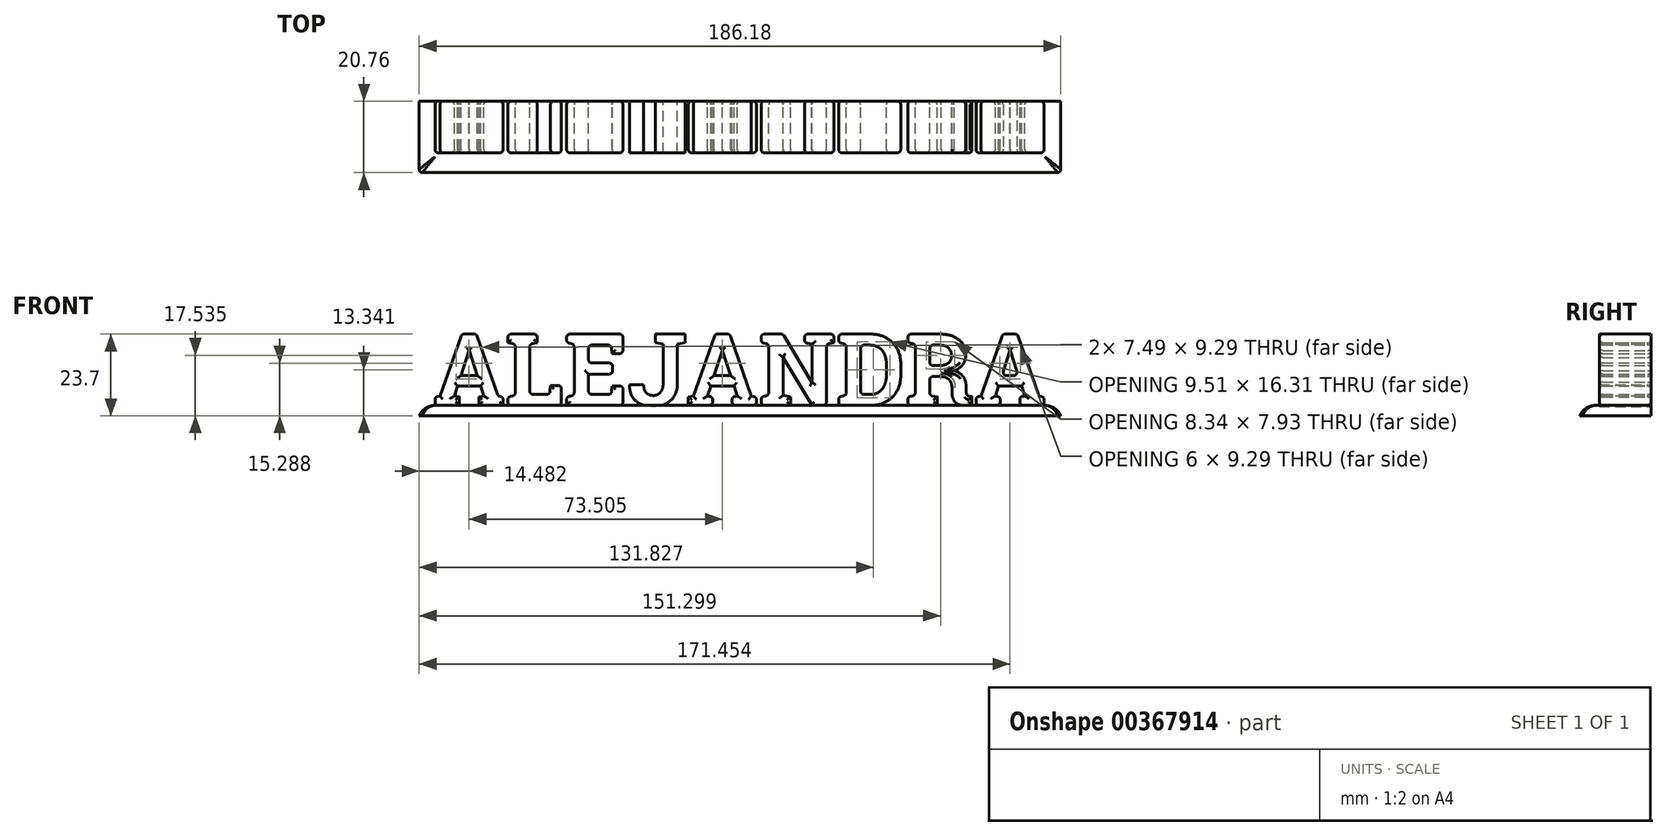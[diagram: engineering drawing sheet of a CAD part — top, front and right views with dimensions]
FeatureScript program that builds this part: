
annotation { "Feature Type Name" : "Feature", "Feature Type Description" : "" }
export const myFeature = defineFeature(function(context is Context, id is Id, definition is map)
    precondition{}
    {
        {
            var Q0;
            Q0=qCreatedBy(makeId("Front.planeOp"),FACE);
            var sketch = newSketch(context, id + "F0", { "sketchPlane" : qUnion([Q0])});
            skText(sketch, "E0", { "text": "ALEJANDRA", "fontName": "RobotoSlab-Bold.ttf"});
            const initialGuessF0  = {"E0": [-0.08954, 0, 1, 0, 0.02096]};
            skSetInitialGuess(sketch, initialGuessF0);
            skSolve(sketch);
        }
        {
            var Q0;
            Q0 = qSketchRegion(id + "F0", true);
            extrude(context, id + "F1", {"entities" : qUnion([Q0]), "depth" : 15 * mm});
        }
        {
            var Q0;
            Q0=makeQuery(id+"F1.opExtrude","SWEPT_FACE",FACE,{"disambiguationData":[OSD([sQuery(id+"F0.wireOp",EDGE,"E0.sketch_text.stroke-42")])]});
            var sketch = newSketch(context, id + "F2", { "sketchPlane" : qUnion([Q0])});
            skLineSegment(sketch, "E1.bottom", {"start": v(-93.56, 20.7) * mm, "end": v(92.62, 20.7) * mm});
            skLineSegment(sketch, "E1.top", {"start": v(-93.56, 0) * mm, "end": v(92.62, 0) * mm});
            skLineSegment(sketch, "E1.left", {"start": v(-93.56, 20.7) * mm, "end": v(-93.56, 0) * mm});
            skLineSegment(sketch, "E1.right", {"start": v(92.62, 20.7) * mm, "end": v(92.62, 0) * mm});
            skSolve(sketch);
        }
        {
            var Q0;
            Q0 = qSketchRegion(id + "F2", true);
            extrude(context, id + "F3", {"entities" : qUnion([Q0]), "depth" : 3 * mm});
        }
        {
            var Q0;
            Q0=makeQuery(id+"F3.opExtrude","CAP_EDGE",EDGE,{"disambiguationData":[OSD([sQuery(id+"F2.wireOp",EDGE,"E1.bottom")])],"isStart":true});
            var Q1;
            Q1=makeQuery(id+"F3.opExtrude","CAP_EDGE",EDGE,{"disambiguationData":[OSD([sQuery(id+"F2.wireOp",EDGE,"E1.right")])],"isStart":true});
            var Q2;
            Q2=makeQuery(id+"F3.opExtrude","CAP_EDGE",EDGE,{"disambiguationData":[OSD([sQuery(id+"F2.wireOp",EDGE,"E1.left")])],"isStart":true});
            fillet(context, id + "F4", {"entities" : qUnion([Q0, Q1, Q2]), "radius" : 5 * mm, "tangentPropagation" : true, "allowEdgeOverflow" : false});
        }
        {
            var Q0;
            Q0=makeQuery(id+"F1.opExtrude","CAP_FACE",FACE,{"disambiguationData":[OSD([sQuery(id+"F0.wireOp",EDGE,"E0.sketch_text.stroke-36"),sQuery(id+"F0.wireOp",EDGE,"E0.sketch_text.stroke-37"),sQuery(id+"F0.wireOp",EDGE,"E0.sketch_text.stroke-38"),sQuery(id+"F0.wireOp",EDGE,"E0.sketch_text.stroke-39"),sQuery(id+"F0.wireOp",EDGE,"E0.sketch_text.stroke-40"),sQuery(id+"F0.wireOp",EDGE,"E0.sketch_text.stroke-41"),sQuery(id+"F0.wireOp",EDGE,"E0.sketch_text.stroke-42"),sQuery(id+"F0.wireOp",EDGE,"E0.sketch_text.stroke-43"),sQuery(id+"F0.wireOp",EDGE,"E0.sketch_text.stroke-44"),sQuery(id+"F0.wireOp",EDGE,"E0.sketch_text.stroke-45"),sQuery(id+"F0.wireOp",EDGE,"E0.sketch_text.stroke-46"),sQuery(id+"F0.wireOp",EDGE,"E0.sketch_text.stroke-47"),sQuery(id+"F0.wireOp",EDGE,"E0.sketch_text.stroke-48"),sQuery(id+"F0.wireOp",EDGE,"E0.sketch_text.stroke-49"),sQuery(id+"F0.wireOp",EDGE,"E0.sketch_text.stroke-50"),sQuery(id+"F0.wireOp",EDGE,"E0.sketch_text.stroke-51"),sQuery(id+"F0.wireOp",EDGE,"E0.sketch_text.stroke-52"),sQuery(id+"F0.wireOp",EDGE,"E0.sketch_text.stroke-53"),sQuery(id+"F0.wireOp",EDGE,"E0.sketch_text.stroke-54"),sQuery(id+"F0.wireOp",EDGE,"E0.sketch_text.stroke-55"),sQuery(id+"F0.wireOp",EDGE,"E0.sketch_text.stroke-56")])],"isStart":false});
            var Q1;
            Q1=makeQuery(id+"F1.opExtrude","CAP_FACE",FACE,{"disambiguationData":[OSD([sQuery(id+"F0.wireOp",EDGE,"E0.sketch_text.stroke-20"),sQuery(id+"F0.wireOp",EDGE,"E0.sketch_text.stroke-21"),sQuery(id+"F0.wireOp",EDGE,"E0.sketch_text.stroke-22"),sQuery(id+"F0.wireOp",EDGE,"E0.sketch_text.stroke-23"),sQuery(id+"F0.wireOp",EDGE,"E0.sketch_text.stroke-24"),sQuery(id+"F0.wireOp",EDGE,"E0.sketch_text.stroke-25"),sQuery(id+"F0.wireOp",EDGE,"E0.sketch_text.stroke-26"),sQuery(id+"F0.wireOp",EDGE,"E0.sketch_text.stroke-27"),sQuery(id+"F0.wireOp",EDGE,"E0.sketch_text.stroke-28"),sQuery(id+"F0.wireOp",EDGE,"E0.sketch_text.stroke-29"),sQuery(id+"F0.wireOp",EDGE,"E0.sketch_text.stroke-30"),sQuery(id+"F0.wireOp",EDGE,"E0.sketch_text.stroke-31"),sQuery(id+"F0.wireOp",EDGE,"E0.sketch_text.stroke-32"),sQuery(id+"F0.wireOp",EDGE,"E0.sketch_text.stroke-33"),sQuery(id+"F0.wireOp",EDGE,"E0.sketch_text.stroke-34"),sQuery(id+"F0.wireOp",EDGE,"E0.sketch_text.stroke-35")])],"isStart":false});
            var Q2;
            Q2=makeQuery(id+"F1.opExtrude","CAP_FACE",FACE,{"disambiguationData":[OSD([sQuery(id+"F0.wireOp",EDGE,"E0.sketch_text.stroke-0"),sQuery(id+"F0.wireOp",EDGE,"E0.sketch_text.stroke-1"),sQuery(id+"F0.wireOp",EDGE,"E0.sketch_text.stroke-2"),sQuery(id+"F0.wireOp",EDGE,"E0.sketch_text.stroke-3"),sQuery(id+"F0.wireOp",EDGE,"E0.sketch_text.stroke-4"),sQuery(id+"F0.wireOp",EDGE,"E0.sketch_text.stroke-5"),sQuery(id+"F0.wireOp",EDGE,"E0.sketch_text.stroke-6"),sQuery(id+"F0.wireOp",EDGE,"E0.sketch_text.stroke-7"),sQuery(id+"F0.wireOp",EDGE,"E0.sketch_text.stroke-8"),sQuery(id+"F0.wireOp",EDGE,"E0.sketch_text.stroke-9"),sQuery(id+"F0.wireOp",EDGE,"E0.sketch_text.stroke-10"),sQuery(id+"F0.wireOp",EDGE,"E0.sketch_text.stroke-11"),sQuery(id+"F0.wireOp",EDGE,"E0.sketch_text.stroke-12"),sQuery(id+"F0.wireOp",EDGE,"E0.sketch_text.stroke-13"),sQuery(id+"F0.wireOp",EDGE,"E0.sketch_text.stroke-14"),sQuery(id+"F0.wireOp",EDGE,"E0.sketch_text.stroke-15"),sQuery(id+"F0.wireOp",EDGE,"E0.sketch_text.stroke-16"),sQuery(id+"F0.wireOp",EDGE,"E0.sketch_text.stroke-17"),sQuery(id+"F0.wireOp",EDGE,"E0.sketch_text.stroke-18"),sQuery(id+"F0.wireOp",EDGE,"E0.sketch_text.stroke-19")])],"isStart":false});
            var Q3;
            Q3=makeQuery(id+"F1.opExtrude","CAP_EDGE",EDGE,{"disambiguationData":[OSD([sQuery(id+"F0.wireOp",EDGE,"E0.sketch_text.stroke-70")])],"isStart":false});
            var Q4;
            Q4=makeQuery(id+"F1.opExtrude","CAP_EDGE",EDGE,{"disambiguationData":[OSD([sQuery(id+"F0.wireOp",EDGE,"E0.sketch_text.stroke-59")])],"isStart":false});
            var Q5;
            Q5=makeQuery(id+"F1.opExtrude","CAP_FACE",FACE,{"disambiguationData":[OSD([sQuery(id+"F0.wireOp",EDGE,"E0.sketch_text.stroke-75"),sQuery(id+"F0.wireOp",EDGE,"E0.sketch_text.stroke-76"),sQuery(id+"F0.wireOp",EDGE,"E0.sketch_text.stroke-77"),sQuery(id+"F0.wireOp",EDGE,"E0.sketch_text.stroke-78"),sQuery(id+"F0.wireOp",EDGE,"E0.sketch_text.stroke-79"),sQuery(id+"F0.wireOp",EDGE,"E0.sketch_text.stroke-80"),sQuery(id+"F0.wireOp",EDGE,"E0.sketch_text.stroke-81"),sQuery(id+"F0.wireOp",EDGE,"E0.sketch_text.stroke-82"),sQuery(id+"F0.wireOp",EDGE,"E0.sketch_text.stroke-83"),sQuery(id+"F0.wireOp",EDGE,"E0.sketch_text.stroke-84"),sQuery(id+"F0.wireOp",EDGE,"E0.sketch_text.stroke-85"),sQuery(id+"F0.wireOp",EDGE,"E0.sketch_text.stroke-86"),sQuery(id+"F0.wireOp",EDGE,"E0.sketch_text.stroke-87"),sQuery(id+"F0.wireOp",EDGE,"E0.sketch_text.stroke-88"),sQuery(id+"F0.wireOp",EDGE,"E0.sketch_text.stroke-89"),sQuery(id+"F0.wireOp",EDGE,"E0.sketch_text.stroke-90"),sQuery(id+"F0.wireOp",EDGE,"E0.sketch_text.stroke-91"),sQuery(id+"F0.wireOp",EDGE,"E0.sketch_text.stroke-92"),sQuery(id+"F0.wireOp",EDGE,"E0.sketch_text.stroke-93"),sQuery(id+"F0.wireOp",EDGE,"E0.sketch_text.stroke-94")])],"isStart":false});
            var Q6;
            Q6=makeQuery(id+"F1.opExtrude","CAP_FACE",FACE,{"disambiguationData":[OSD([sQuery(id+"F0.wireOp",EDGE,"E0.sketch_text.stroke-95"),sQuery(id+"F0.wireOp",EDGE,"E0.sketch_text.stroke-96"),sQuery(id+"F0.wireOp",EDGE,"E0.sketch_text.stroke-97"),sQuery(id+"F0.wireOp",EDGE,"E0.sketch_text.stroke-98"),sQuery(id+"F0.wireOp",EDGE,"E0.sketch_text.stroke-99"),sQuery(id+"F0.wireOp",EDGE,"E0.sketch_text.stroke-100"),sQuery(id+"F0.wireOp",EDGE,"E0.sketch_text.stroke-101"),sQuery(id+"F0.wireOp",EDGE,"E0.sketch_text.stroke-102"),sQuery(id+"F0.wireOp",EDGE,"E0.sketch_text.stroke-103"),sQuery(id+"F0.wireOp",EDGE,"E0.sketch_text.stroke-104"),sQuery(id+"F0.wireOp",EDGE,"E0.sketch_text.stroke-105"),sQuery(id+"F0.wireOp",EDGE,"E0.sketch_text.stroke-106"),sQuery(id+"F0.wireOp",EDGE,"E0.sketch_text.stroke-107"),sQuery(id+"F0.wireOp",EDGE,"E0.sketch_text.stroke-108"),sQuery(id+"F0.wireOp",EDGE,"E0.sketch_text.stroke-109"),sQuery(id+"F0.wireOp",EDGE,"E0.sketch_text.stroke-110"),sQuery(id+"F0.wireOp",EDGE,"E0.sketch_text.stroke-111"),sQuery(id+"F0.wireOp",EDGE,"E0.sketch_text.stroke-112"),sQuery(id+"F0.wireOp",EDGE,"E0.sketch_text.stroke-113"),sQuery(id+"F0.wireOp",EDGE,"E0.sketch_text.stroke-114"),sQuery(id+"F0.wireOp",EDGE,"E0.sketch_text.stroke-115"),sQuery(id+"F0.wireOp",EDGE,"E0.sketch_text.stroke-116"),sQuery(id+"F0.wireOp",EDGE,"E0.sketch_text.stroke-117"),sQuery(id+"F0.wireOp",EDGE,"E0.sketch_text.stroke-118")])],"isStart":false});
            var Q7;
            Q7=makeQuery(id+"F1.opExtrude","CAP_FACE",FACE,{"disambiguationData":[OSD([sQuery(id+"F0.wireOp",EDGE,"E0.sketch_text.stroke-119"),sQuery(id+"F0.wireOp",EDGE,"E0.sketch_text.stroke-120"),sQuery(id+"F0.wireOp",EDGE,"E0.sketch_text.stroke-121"),sQuery(id+"F0.wireOp",EDGE,"E0.sketch_text.stroke-122"),sQuery(id+"F0.wireOp",EDGE,"E0.sketch_text.stroke-123"),sQuery(id+"F0.wireOp",EDGE,"E0.sketch_text.stroke-124"),sQuery(id+"F0.wireOp",EDGE,"E0.sketch_text.stroke-125"),sQuery(id+"F0.wireOp",EDGE,"E0.sketch_text.stroke-126"),sQuery(id+"F0.wireOp",EDGE,"E0.sketch_text.stroke-127"),sQuery(id+"F0.wireOp",EDGE,"E0.sketch_text.stroke-128"),sQuery(id+"F0.wireOp",EDGE,"E0.sketch_text.stroke-129"),sQuery(id+"F0.wireOp",EDGE,"E0.sketch_text.stroke-130"),sQuery(id+"F0.wireOp",EDGE,"E0.sketch_text.stroke-131"),sQuery(id+"F0.wireOp",EDGE,"E0.sketch_text.stroke-132"),sQuery(id+"F0.wireOp",EDGE,"E0.sketch_text.stroke-133"),sQuery(id+"F0.wireOp",EDGE,"E0.sketch_text.stroke-134"),sQuery(id+"F0.wireOp",EDGE,"E0.sketch_text.stroke-135"),sQuery(id+"F0.wireOp",EDGE,"E0.sketch_text.stroke-136"),sQuery(id+"F0.wireOp",EDGE,"E0.sketch_text.stroke-137"),sQuery(id+"F0.wireOp",EDGE,"E0.sketch_text.stroke-138"),sQuery(id+"F0.wireOp",EDGE,"E0.sketch_text.stroke-139")])],"isStart":false});
            var Q8;
            Q8=makeQuery(id+"F1.opExtrude","CAP_FACE",FACE,{"disambiguationData":[OSD([sQuery(id+"F0.wireOp",EDGE,"E0.sketch_text.stroke-140"),sQuery(id+"F0.wireOp",EDGE,"E0.sketch_text.stroke-141"),sQuery(id+"F0.wireOp",EDGE,"E0.sketch_text.stroke-142"),sQuery(id+"F0.wireOp",EDGE,"E0.sketch_text.stroke-143"),sQuery(id+"F0.wireOp",EDGE,"E0.sketch_text.stroke-144"),sQuery(id+"F0.wireOp",EDGE,"E0.sketch_text.stroke-145"),sQuery(id+"F0.wireOp",EDGE,"E0.sketch_text.stroke-146"),sQuery(id+"F0.wireOp",EDGE,"E0.sketch_text.stroke-147"),sQuery(id+"F0.wireOp",EDGE,"E0.sketch_text.stroke-148"),sQuery(id+"F0.wireOp",EDGE,"E0.sketch_text.stroke-149"),sQuery(id+"F0.wireOp",EDGE,"E0.sketch_text.stroke-150"),sQuery(id+"F0.wireOp",EDGE,"E0.sketch_text.stroke-151"),sQuery(id+"F0.wireOp",EDGE,"E0.sketch_text.stroke-152"),sQuery(id+"F0.wireOp",EDGE,"E0.sketch_text.stroke-153"),sQuery(id+"F0.wireOp",EDGE,"E0.sketch_text.stroke-154"),sQuery(id+"F0.wireOp",EDGE,"E0.sketch_text.stroke-155"),sQuery(id+"F0.wireOp",EDGE,"E0.sketch_text.stroke-156"),sQuery(id+"F0.wireOp",EDGE,"E0.sketch_text.stroke-157"),sQuery(id+"F0.wireOp",EDGE,"E0.sketch_text.stroke-158"),sQuery(id+"F0.wireOp",EDGE,"E0.sketch_text.stroke-159"),sQuery(id+"F0.wireOp",EDGE,"E0.sketch_text.stroke-160"),sQuery(id+"F0.wireOp",EDGE,"E0.sketch_text.stroke-161"),sQuery(id+"F0.wireOp",EDGE,"E0.sketch_text.stroke-162"),sQuery(id+"F0.wireOp",EDGE,"E0.sketch_text.stroke-163"),sQuery(id+"F0.wireOp",EDGE,"E0.sketch_text.stroke-164"),sQuery(id+"F0.wireOp",EDGE,"E0.sketch_text.stroke-165"),sQuery(id+"F0.wireOp",EDGE,"E0.sketch_text.stroke-166"),sQuery(id+"F0.wireOp",EDGE,"E0.sketch_text.stroke-167"),sQuery(id+"F0.wireOp",EDGE,"E0.sketch_text.stroke-168"),sQuery(id+"F0.wireOp",EDGE,"E0.sketch_text.stroke-169"),sQuery(id+"F0.wireOp",EDGE,"E0.sketch_text.stroke-170"),sQuery(id+"F0.wireOp",EDGE,"E0.sketch_text.stroke-171"),sQuery(id+"F0.wireOp",EDGE,"E0.sketch_text.stroke-172"),sQuery(id+"F0.wireOp",EDGE,"E0.sketch_text.stroke-173"),sQuery(id+"F0.wireOp",EDGE,"E0.sketch_text.stroke-174"),sQuery(id+"F0.wireOp",EDGE,"E0.sketch_text.stroke-175")])],"isStart":false});
            var Q9;
            Q9=makeQuery(id+"F1.opExtrude","CAP_FACE",FACE,{"disambiguationData":[OSD([sQuery(id+"F0.wireOp",EDGE,"E0.sketch_text.stroke-176"),sQuery(id+"F0.wireOp",EDGE,"E0.sketch_text.stroke-177"),sQuery(id+"F0.wireOp",EDGE,"E0.sketch_text.stroke-178"),sQuery(id+"F0.wireOp",EDGE,"E0.sketch_text.stroke-179"),sQuery(id+"F0.wireOp",EDGE,"E0.sketch_text.stroke-180"),sQuery(id+"F0.wireOp",EDGE,"E0.sketch_text.stroke-181"),sQuery(id+"F0.wireOp",EDGE,"E0.sketch_text.stroke-182"),sQuery(id+"F0.wireOp",EDGE,"E0.sketch_text.stroke-183"),sQuery(id+"F0.wireOp",EDGE,"E0.sketch_text.stroke-184"),sQuery(id+"F0.wireOp",EDGE,"E0.sketch_text.stroke-185"),sQuery(id+"F0.wireOp",EDGE,"E0.sketch_text.stroke-186"),sQuery(id+"F0.wireOp",EDGE,"E0.sketch_text.stroke-187"),sQuery(id+"F0.wireOp",EDGE,"E0.sketch_text.stroke-188"),sQuery(id+"F0.wireOp",EDGE,"E0.sketch_text.stroke-189"),sQuery(id+"F0.wireOp",EDGE,"E0.sketch_text.stroke-190"),sQuery(id+"F0.wireOp",EDGE,"E0.sketch_text.stroke-191"),sQuery(id+"F0.wireOp",EDGE,"E0.sketch_text.stroke-192"),sQuery(id+"F0.wireOp",EDGE,"E0.sketch_text.stroke-193"),sQuery(id+"F0.wireOp",EDGE,"E0.sketch_text.stroke-194"),sQuery(id+"F0.wireOp",EDGE,"E0.sketch_text.stroke-195")])],"isStart":false});
            var Q10;
            Q10=makeQuery(id+"F1.opExtrude","CAP_FACE",FACE,{"disambiguationData":[OSD([sQuery(id+"F0.wireOp",EDGE,"E0.sketch_text.stroke-0"),sQuery(id+"F0.wireOp",EDGE,"E0.sketch_text.stroke-1"),sQuery(id+"F0.wireOp",EDGE,"E0.sketch_text.stroke-2"),sQuery(id+"F0.wireOp",EDGE,"E0.sketch_text.stroke-3"),sQuery(id+"F0.wireOp",EDGE,"E0.sketch_text.stroke-4"),sQuery(id+"F0.wireOp",EDGE,"E0.sketch_text.stroke-5"),sQuery(id+"F0.wireOp",EDGE,"E0.sketch_text.stroke-6"),sQuery(id+"F0.wireOp",EDGE,"E0.sketch_text.stroke-7"),sQuery(id+"F0.wireOp",EDGE,"E0.sketch_text.stroke-8"),sQuery(id+"F0.wireOp",EDGE,"E0.sketch_text.stroke-9"),sQuery(id+"F0.wireOp",EDGE,"E0.sketch_text.stroke-10"),sQuery(id+"F0.wireOp",EDGE,"E0.sketch_text.stroke-11"),sQuery(id+"F0.wireOp",EDGE,"E0.sketch_text.stroke-12"),sQuery(id+"F0.wireOp",EDGE,"E0.sketch_text.stroke-13"),sQuery(id+"F0.wireOp",EDGE,"E0.sketch_text.stroke-14"),sQuery(id+"F0.wireOp",EDGE,"E0.sketch_text.stroke-15"),sQuery(id+"F0.wireOp",EDGE,"E0.sketch_text.stroke-16"),sQuery(id+"F0.wireOp",EDGE,"E0.sketch_text.stroke-17"),sQuery(id+"F0.wireOp",EDGE,"E0.sketch_text.stroke-18"),sQuery(id+"F0.wireOp",EDGE,"E0.sketch_text.stroke-19")])],"isStart":true});
            var Q11;
            Q11=makeQuery(id+"F1.opExtrude","CAP_FACE",FACE,{"disambiguationData":[OSD([sQuery(id+"F0.wireOp",EDGE,"E0.sketch_text.stroke-20"),sQuery(id+"F0.wireOp",EDGE,"E0.sketch_text.stroke-21"),sQuery(id+"F0.wireOp",EDGE,"E0.sketch_text.stroke-22"),sQuery(id+"F0.wireOp",EDGE,"E0.sketch_text.stroke-23"),sQuery(id+"F0.wireOp",EDGE,"E0.sketch_text.stroke-24"),sQuery(id+"F0.wireOp",EDGE,"E0.sketch_text.stroke-25"),sQuery(id+"F0.wireOp",EDGE,"E0.sketch_text.stroke-26"),sQuery(id+"F0.wireOp",EDGE,"E0.sketch_text.stroke-27"),sQuery(id+"F0.wireOp",EDGE,"E0.sketch_text.stroke-28"),sQuery(id+"F0.wireOp",EDGE,"E0.sketch_text.stroke-29"),sQuery(id+"F0.wireOp",EDGE,"E0.sketch_text.stroke-30"),sQuery(id+"F0.wireOp",EDGE,"E0.sketch_text.stroke-31"),sQuery(id+"F0.wireOp",EDGE,"E0.sketch_text.stroke-32"),sQuery(id+"F0.wireOp",EDGE,"E0.sketch_text.stroke-33"),sQuery(id+"F0.wireOp",EDGE,"E0.sketch_text.stroke-34"),sQuery(id+"F0.wireOp",EDGE,"E0.sketch_text.stroke-35")])],"isStart":true});
            var Q12;
            Q12=makeQuery(id+"F1.opExtrude","CAP_FACE",FACE,{"disambiguationData":[OSD([sQuery(id+"F0.wireOp",EDGE,"E0.sketch_text.stroke-36"),sQuery(id+"F0.wireOp",EDGE,"E0.sketch_text.stroke-37"),sQuery(id+"F0.wireOp",EDGE,"E0.sketch_text.stroke-38"),sQuery(id+"F0.wireOp",EDGE,"E0.sketch_text.stroke-39"),sQuery(id+"F0.wireOp",EDGE,"E0.sketch_text.stroke-40"),sQuery(id+"F0.wireOp",EDGE,"E0.sketch_text.stroke-41"),sQuery(id+"F0.wireOp",EDGE,"E0.sketch_text.stroke-42"),sQuery(id+"F0.wireOp",EDGE,"E0.sketch_text.stroke-43"),sQuery(id+"F0.wireOp",EDGE,"E0.sketch_text.stroke-44"),sQuery(id+"F0.wireOp",EDGE,"E0.sketch_text.stroke-45"),sQuery(id+"F0.wireOp",EDGE,"E0.sketch_text.stroke-46"),sQuery(id+"F0.wireOp",EDGE,"E0.sketch_text.stroke-47"),sQuery(id+"F0.wireOp",EDGE,"E0.sketch_text.stroke-48"),sQuery(id+"F0.wireOp",EDGE,"E0.sketch_text.stroke-49"),sQuery(id+"F0.wireOp",EDGE,"E0.sketch_text.stroke-50"),sQuery(id+"F0.wireOp",EDGE,"E0.sketch_text.stroke-51"),sQuery(id+"F0.wireOp",EDGE,"E0.sketch_text.stroke-52"),sQuery(id+"F0.wireOp",EDGE,"E0.sketch_text.stroke-53"),sQuery(id+"F0.wireOp",EDGE,"E0.sketch_text.stroke-54"),sQuery(id+"F0.wireOp",EDGE,"E0.sketch_text.stroke-55"),sQuery(id+"F0.wireOp",EDGE,"E0.sketch_text.stroke-56")])],"isStart":true});
            var Q13;
            Q13=makeQuery(id+"F1.opExtrude","CAP_FACE",FACE,{"disambiguationData":[OSD([sQuery(id+"F0.wireOp",EDGE,"E0.sketch_text.stroke-57"),sQuery(id+"F0.wireOp",EDGE,"E0.sketch_text.stroke-58"),sQuery(id+"F0.wireOp",EDGE,"E0.sketch_text.stroke-59"),sQuery(id+"F0.wireOp",EDGE,"E0.sketch_text.stroke-60"),sQuery(id+"F0.wireOp",EDGE,"E0.sketch_text.stroke-61"),sQuery(id+"F0.wireOp",EDGE,"E0.sketch_text.stroke-62"),sQuery(id+"F0.wireOp",EDGE,"E0.sketch_text.stroke-63"),sQuery(id+"F0.wireOp",EDGE,"E0.sketch_text.stroke-64"),sQuery(id+"F0.wireOp",EDGE,"E0.sketch_text.stroke-65"),sQuery(id+"F0.wireOp",EDGE,"E0.sketch_text.stroke-66"),sQuery(id+"F0.wireOp",EDGE,"E0.sketch_text.stroke-67"),sQuery(id+"F0.wireOp",EDGE,"E0.sketch_text.stroke-68"),sQuery(id+"F0.wireOp",EDGE,"E0.sketch_text.stroke-69"),sQuery(id+"F0.wireOp",EDGE,"E0.sketch_text.stroke-70"),sQuery(id+"F0.wireOp",EDGE,"E0.sketch_text.stroke-71"),sQuery(id+"F0.wireOp",EDGE,"E0.sketch_text.stroke-72"),sQuery(id+"F0.wireOp",EDGE,"E0.sketch_text.stroke-73"),sQuery(id+"F0.wireOp",EDGE,"E0.sketch_text.stroke-74")])],"isStart":true});
            var Q14;
            Q14=makeQuery(id+"F1.opExtrude","CAP_FACE",FACE,{"disambiguationData":[OSD([sQuery(id+"F0.wireOp",EDGE,"E0.sketch_text.stroke-75"),sQuery(id+"F0.wireOp",EDGE,"E0.sketch_text.stroke-76"),sQuery(id+"F0.wireOp",EDGE,"E0.sketch_text.stroke-77"),sQuery(id+"F0.wireOp",EDGE,"E0.sketch_text.stroke-78"),sQuery(id+"F0.wireOp",EDGE,"E0.sketch_text.stroke-79"),sQuery(id+"F0.wireOp",EDGE,"E0.sketch_text.stroke-80"),sQuery(id+"F0.wireOp",EDGE,"E0.sketch_text.stroke-81"),sQuery(id+"F0.wireOp",EDGE,"E0.sketch_text.stroke-82"),sQuery(id+"F0.wireOp",EDGE,"E0.sketch_text.stroke-83"),sQuery(id+"F0.wireOp",EDGE,"E0.sketch_text.stroke-84"),sQuery(id+"F0.wireOp",EDGE,"E0.sketch_text.stroke-85"),sQuery(id+"F0.wireOp",EDGE,"E0.sketch_text.stroke-86"),sQuery(id+"F0.wireOp",EDGE,"E0.sketch_text.stroke-87"),sQuery(id+"F0.wireOp",EDGE,"E0.sketch_text.stroke-88"),sQuery(id+"F0.wireOp",EDGE,"E0.sketch_text.stroke-89"),sQuery(id+"F0.wireOp",EDGE,"E0.sketch_text.stroke-90"),sQuery(id+"F0.wireOp",EDGE,"E0.sketch_text.stroke-91"),sQuery(id+"F0.wireOp",EDGE,"E0.sketch_text.stroke-92"),sQuery(id+"F0.wireOp",EDGE,"E0.sketch_text.stroke-93"),sQuery(id+"F0.wireOp",EDGE,"E0.sketch_text.stroke-94")])],"isStart":true});
            var Q15;
            Q15=makeQuery(id+"F1.opExtrude","CAP_FACE",FACE,{"disambiguationData":[OSD([sQuery(id+"F0.wireOp",EDGE,"E0.sketch_text.stroke-95"),sQuery(id+"F0.wireOp",EDGE,"E0.sketch_text.stroke-96"),sQuery(id+"F0.wireOp",EDGE,"E0.sketch_text.stroke-97"),sQuery(id+"F0.wireOp",EDGE,"E0.sketch_text.stroke-98"),sQuery(id+"F0.wireOp",EDGE,"E0.sketch_text.stroke-99"),sQuery(id+"F0.wireOp",EDGE,"E0.sketch_text.stroke-100"),sQuery(id+"F0.wireOp",EDGE,"E0.sketch_text.stroke-101"),sQuery(id+"F0.wireOp",EDGE,"E0.sketch_text.stroke-102"),sQuery(id+"F0.wireOp",EDGE,"E0.sketch_text.stroke-103"),sQuery(id+"F0.wireOp",EDGE,"E0.sketch_text.stroke-104"),sQuery(id+"F0.wireOp",EDGE,"E0.sketch_text.stroke-105"),sQuery(id+"F0.wireOp",EDGE,"E0.sketch_text.stroke-106"),sQuery(id+"F0.wireOp",EDGE,"E0.sketch_text.stroke-107"),sQuery(id+"F0.wireOp",EDGE,"E0.sketch_text.stroke-108"),sQuery(id+"F0.wireOp",EDGE,"E0.sketch_text.stroke-109"),sQuery(id+"F0.wireOp",EDGE,"E0.sketch_text.stroke-110"),sQuery(id+"F0.wireOp",EDGE,"E0.sketch_text.stroke-111"),sQuery(id+"F0.wireOp",EDGE,"E0.sketch_text.stroke-112"),sQuery(id+"F0.wireOp",EDGE,"E0.sketch_text.stroke-113"),sQuery(id+"F0.wireOp",EDGE,"E0.sketch_text.stroke-114"),sQuery(id+"F0.wireOp",EDGE,"E0.sketch_text.stroke-115"),sQuery(id+"F0.wireOp",EDGE,"E0.sketch_text.stroke-116"),sQuery(id+"F0.wireOp",EDGE,"E0.sketch_text.stroke-117"),sQuery(id+"F0.wireOp",EDGE,"E0.sketch_text.stroke-118")])],"isStart":true});
            var Q16;
            Q16=makeQuery(id+"F1.opExtrude","CAP_FACE",FACE,{"disambiguationData":[OSD([sQuery(id+"F0.wireOp",EDGE,"E0.sketch_text.stroke-119"),sQuery(id+"F0.wireOp",EDGE,"E0.sketch_text.stroke-120"),sQuery(id+"F0.wireOp",EDGE,"E0.sketch_text.stroke-121"),sQuery(id+"F0.wireOp",EDGE,"E0.sketch_text.stroke-122"),sQuery(id+"F0.wireOp",EDGE,"E0.sketch_text.stroke-123"),sQuery(id+"F0.wireOp",EDGE,"E0.sketch_text.stroke-124"),sQuery(id+"F0.wireOp",EDGE,"E0.sketch_text.stroke-125"),sQuery(id+"F0.wireOp",EDGE,"E0.sketch_text.stroke-126"),sQuery(id+"F0.wireOp",EDGE,"E0.sketch_text.stroke-127"),sQuery(id+"F0.wireOp",EDGE,"E0.sketch_text.stroke-128"),sQuery(id+"F0.wireOp",EDGE,"E0.sketch_text.stroke-129"),sQuery(id+"F0.wireOp",EDGE,"E0.sketch_text.stroke-130"),sQuery(id+"F0.wireOp",EDGE,"E0.sketch_text.stroke-131"),sQuery(id+"F0.wireOp",EDGE,"E0.sketch_text.stroke-132"),sQuery(id+"F0.wireOp",EDGE,"E0.sketch_text.stroke-133"),sQuery(id+"F0.wireOp",EDGE,"E0.sketch_text.stroke-134"),sQuery(id+"F0.wireOp",EDGE,"E0.sketch_text.stroke-135"),sQuery(id+"F0.wireOp",EDGE,"E0.sketch_text.stroke-136"),sQuery(id+"F0.wireOp",EDGE,"E0.sketch_text.stroke-137"),sQuery(id+"F0.wireOp",EDGE,"E0.sketch_text.stroke-138"),sQuery(id+"F0.wireOp",EDGE,"E0.sketch_text.stroke-139")])],"isStart":true});
            var Q17;
            Q17=makeQuery(id+"F1.opExtrude","CAP_FACE",FACE,{"disambiguationData":[OSD([sQuery(id+"F0.wireOp",EDGE,"E0.sketch_text.stroke-140"),sQuery(id+"F0.wireOp",EDGE,"E0.sketch_text.stroke-141"),sQuery(id+"F0.wireOp",EDGE,"E0.sketch_text.stroke-142"),sQuery(id+"F0.wireOp",EDGE,"E0.sketch_text.stroke-143"),sQuery(id+"F0.wireOp",EDGE,"E0.sketch_text.stroke-144"),sQuery(id+"F0.wireOp",EDGE,"E0.sketch_text.stroke-145"),sQuery(id+"F0.wireOp",EDGE,"E0.sketch_text.stroke-146"),sQuery(id+"F0.wireOp",EDGE,"E0.sketch_text.stroke-147"),sQuery(id+"F0.wireOp",EDGE,"E0.sketch_text.stroke-148"),sQuery(id+"F0.wireOp",EDGE,"E0.sketch_text.stroke-149"),sQuery(id+"F0.wireOp",EDGE,"E0.sketch_text.stroke-150"),sQuery(id+"F0.wireOp",EDGE,"E0.sketch_text.stroke-151"),sQuery(id+"F0.wireOp",EDGE,"E0.sketch_text.stroke-152"),sQuery(id+"F0.wireOp",EDGE,"E0.sketch_text.stroke-153"),sQuery(id+"F0.wireOp",EDGE,"E0.sketch_text.stroke-154"),sQuery(id+"F0.wireOp",EDGE,"E0.sketch_text.stroke-155"),sQuery(id+"F0.wireOp",EDGE,"E0.sketch_text.stroke-156"),sQuery(id+"F0.wireOp",EDGE,"E0.sketch_text.stroke-157"),sQuery(id+"F0.wireOp",EDGE,"E0.sketch_text.stroke-158"),sQuery(id+"F0.wireOp",EDGE,"E0.sketch_text.stroke-159"),sQuery(id+"F0.wireOp",EDGE,"E0.sketch_text.stroke-160"),sQuery(id+"F0.wireOp",EDGE,"E0.sketch_text.stroke-161"),sQuery(id+"F0.wireOp",EDGE,"E0.sketch_text.stroke-162"),sQuery(id+"F0.wireOp",EDGE,"E0.sketch_text.stroke-163"),sQuery(id+"F0.wireOp",EDGE,"E0.sketch_text.stroke-164"),sQuery(id+"F0.wireOp",EDGE,"E0.sketch_text.stroke-165"),sQuery(id+"F0.wireOp",EDGE,"E0.sketch_text.stroke-166"),sQuery(id+"F0.wireOp",EDGE,"E0.sketch_text.stroke-167"),sQuery(id+"F0.wireOp",EDGE,"E0.sketch_text.stroke-168"),sQuery(id+"F0.wireOp",EDGE,"E0.sketch_text.stroke-169"),sQuery(id+"F0.wireOp",EDGE,"E0.sketch_text.stroke-170"),sQuery(id+"F0.wireOp",EDGE,"E0.sketch_text.stroke-171"),sQuery(id+"F0.wireOp",EDGE,"E0.sketch_text.stroke-172"),sQuery(id+"F0.wireOp",EDGE,"E0.sketch_text.stroke-173"),sQuery(id+"F0.wireOp",EDGE,"E0.sketch_text.stroke-174"),sQuery(id+"F0.wireOp",EDGE,"E0.sketch_text.stroke-175")])],"isStart":true});
            var Q18;
            Q18=makeQuery(id+"F1.opExtrude","CAP_FACE",FACE,{"disambiguationData":[OSD([sQuery(id+"F0.wireOp",EDGE,"E0.sketch_text.stroke-176"),sQuery(id+"F0.wireOp",EDGE,"E0.sketch_text.stroke-177"),sQuery(id+"F0.wireOp",EDGE,"E0.sketch_text.stroke-178"),sQuery(id+"F0.wireOp",EDGE,"E0.sketch_text.stroke-179"),sQuery(id+"F0.wireOp",EDGE,"E0.sketch_text.stroke-180"),sQuery(id+"F0.wireOp",EDGE,"E0.sketch_text.stroke-181"),sQuery(id+"F0.wireOp",EDGE,"E0.sketch_text.stroke-182"),sQuery(id+"F0.wireOp",EDGE,"E0.sketch_text.stroke-183"),sQuery(id+"F0.wireOp",EDGE,"E0.sketch_text.stroke-184"),sQuery(id+"F0.wireOp",EDGE,"E0.sketch_text.stroke-185"),sQuery(id+"F0.wireOp",EDGE,"E0.sketch_text.stroke-186"),sQuery(id+"F0.wireOp",EDGE,"E0.sketch_text.stroke-187"),sQuery(id+"F0.wireOp",EDGE,"E0.sketch_text.stroke-188"),sQuery(id+"F0.wireOp",EDGE,"E0.sketch_text.stroke-189"),sQuery(id+"F0.wireOp",EDGE,"E0.sketch_text.stroke-190"),sQuery(id+"F0.wireOp",EDGE,"E0.sketch_text.stroke-191"),sQuery(id+"F0.wireOp",EDGE,"E0.sketch_text.stroke-192"),sQuery(id+"F0.wireOp",EDGE,"E0.sketch_text.stroke-193"),sQuery(id+"F0.wireOp",EDGE,"E0.sketch_text.stroke-194"),sQuery(id+"F0.wireOp",EDGE,"E0.sketch_text.stroke-195")])],"isStart":true});
            var Q19;
            Q19=makeQuery(id+"F1.opExtrude","SWEPT_FACE",FACE,{"disambiguationData":[OSD([sQuery(id+"F0.wireOp",EDGE,"E0.sketch_text.stroke-56")])]});
            var Q20;
            Q20=makeQuery(id+"F1.opExtrude","SWEPT_FACE",FACE,{"disambiguationData":[OSD([sQuery(id+"F0.wireOp",EDGE,"E0.sketch_text.stroke-50")])]});
            var Q21;
            Q21=makeQuery(id+"F1.opExtrude","SWEPT_FACE",FACE,{"disambiguationData":[OSD([sQuery(id+"F0.wireOp",EDGE,"E0.sketch_text.stroke-41")])]});
            var Q22;
            Q22=makeQuery(id+"F1.opExtrude","SWEPT_FACE",FACE,{"disambiguationData":[OSD([sQuery(id+"F0.wireOp",EDGE,"E0.sketch_text.stroke-38")])]});
            var Q23;
            Q23=makeQuery(id+"F1.opExtrude","SWEPT_FACE",FACE,{"disambiguationData":[OSD([sQuery(id+"F0.wireOp",EDGE,"E0.sketch_text.stroke-55")])]});
            var Q24;
            Q24=makeQuery(id+"F1.opExtrude","SWEPT_FACE",FACE,{"disambiguationData":[OSD([sQuery(id+"F0.wireOp",EDGE,"E0.sketch_text.stroke-53")])]});
            var Q25;
            Q25=makeQuery(id+"F1.opExtrude","SWEPT_FACE",FACE,{"disambiguationData":[OSD([sQuery(id+"F0.wireOp",EDGE,"E0.sketch_text.stroke-31")])]});
            var Q26;
            Q26=makeQuery(id+"F1.opExtrude","SWEPT_FACE",FACE,{"disambiguationData":[OSD([sQuery(id+"F0.wireOp",EDGE,"E0.sketch_text.stroke-30")])]});
            var Q27;
            Q27=makeQuery(id+"F1.opExtrude","SWEPT_FACE",FACE,{"disambiguationData":[OSD([sQuery(id+"F0.wireOp",EDGE,"E0.sketch_text.stroke-25"),sQuery(id+"F0.wireOp",EDGE,"E0.sketch_text.stroke-26"),sQuery(id+"F0.wireOp",EDGE,"E0.sketch_text.stroke-27")])]});
            var Q28;
            Q28=makeQuery(id+"F1.opExtrude","SWEPT_FACE",FACE,{"disambiguationData":[OSD([sQuery(id+"F0.wireOp",EDGE,"E0.sketch_text.stroke-34")])]});
            var Q29;
            Q29=makeQuery(id+"F1.opExtrude","SWEPT_FACE",FACE,{"disambiguationData":[OSD([sQuery(id+"F0.wireOp",EDGE,"E0.sketch_text.stroke-22")])]});
            var Q30;
            Q30=makeQuery(id+"F1.opExtrude","SWEPT_FACE",FACE,{"disambiguationData":[OSD([sQuery(id+"F0.wireOp",EDGE,"E0.sketch_text.stroke-20")])]});
            var Q31;
            Q31=makeQuery(id+"F1.opExtrude","SWEPT_FACE",FACE,{"disambiguationData":[OSD([sQuery(id+"F0.wireOp",EDGE,"E0.sketch_text.stroke-15")])]});
            var Q32;
            Q32=makeQuery(id+"F1.opExtrude","SWEPT_FACE",FACE,{"disambiguationData":[OSD([sQuery(id+"F0.wireOp",EDGE,"E0.sketch_text.stroke-2")])]});
            var Q33;
            Q33=makeQuery(id+"F1.opExtrude","SWEPT_FACE",FACE,{"disambiguationData":[OSD([sQuery(id+"F0.wireOp",EDGE,"E0.sketch_text.stroke-4")])]});
            var Q34;
            Q34=makeQuery(id+"F1.opExtrude","SWEPT_FACE",FACE,{"disambiguationData":[OSD([sQuery(id+"F0.wireOp",EDGE,"E0.sketch_text.stroke-44")])]});
            var Q35;
            Q35=makeQuery(id+"F1.opExtrude","SWEPT_FACE",FACE,{"disambiguationData":[OSD([sQuery(id+"F0.wireOp",EDGE,"E0.sketch_text.stroke-45")])]});
            var Q36;
            Q36=makeQuery(id+"F1.opExtrude","SWEPT_FACE",FACE,{"disambiguationData":[OSD([sQuery(id+"F0.wireOp",EDGE,"E0.sketch_text.stroke-47")])]});
            var Q37;
            Q37=makeQuery(id+"F1.opExtrude","SWEPT_FACE",FACE,{"disambiguationData":[OSD([sQuery(id+"F0.wireOp",EDGE,"E0.sketch_text.stroke-70")])]});
            var Q38;
            Q38=makeQuery(id+"F1.opExtrude","SWEPT_FACE",FACE,{"disambiguationData":[OSD([sQuery(id+"F0.wireOp",EDGE,"E0.sketch_text.stroke-72")])]});
            var Q39;
            Q39=makeQuery(id+"F1.opExtrude","SWEPT_FACE",FACE,{"disambiguationData":[OSD([sQuery(id+"F0.wireOp",EDGE,"E0.sketch_text.stroke-73"),sQuery(id+"F0.wireOp",EDGE,"E0.sketch_text.stroke-74")])]});
            var Q40;
            Q40=makeQuery(id+"F1.opExtrude","SWEPT_FACE",FACE,{"disambiguationData":[OSD([sQuery(id+"F0.wireOp",EDGE,"E0.sketch_text.stroke-57")])]});
            var Q41;
            Q41=makeQuery(id+"F1.opExtrude","SWEPT_FACE",FACE,{"disambiguationData":[OSD([sQuery(id+"F0.wireOp",EDGE,"E0.sketch_text.stroke-59")])]});
            var Q42;
            Q42=makeQuery(id+"F1.opExtrude","SWEPT_FACE",FACE,{"disambiguationData":[OSD([sQuery(id+"F0.wireOp",EDGE,"E0.sketch_text.stroke-88")])]});
            var Q43;
            Q43=makeQuery(id+"F1.opExtrude","SWEPT_FACE",FACE,{"disambiguationData":[OSD([sQuery(id+"F0.wireOp",EDGE,"E0.sketch_text.stroke-82")])]});
            var Q44;
            Q44=makeQuery(id+"F1.opExtrude","SWEPT_FACE",FACE,{"disambiguationData":[OSD([sQuery(id+"F0.wireOp",EDGE,"E0.sketch_text.stroke-80")])]});
            var Q45;
            Q45=makeQuery(id+"F1.opExtrude","SWEPT_FACE",FACE,{"disambiguationData":[OSD([sQuery(id+"F0.wireOp",EDGE,"E0.sketch_text.stroke-77")])]});
            var Q46;
            Q46=makeQuery(id+"F1.opExtrude","SWEPT_FACE",FACE,{"disambiguationData":[OSD([sQuery(id+"F0.wireOp",EDGE,"E0.sketch_text.stroke-107")])]});
            var Q47;
            Q47=makeQuery(id+"F1.opExtrude","SWEPT_FACE",FACE,{"disambiguationData":[OSD([sQuery(id+"F0.wireOp",EDGE,"E0.sketch_text.stroke-109")])]});
            var Q48;
            Q48=makeQuery(id+"F1.opExtrude","SWEPT_FACE",FACE,{"disambiguationData":[OSD([sQuery(id+"F0.wireOp",EDGE,"E0.sketch_text.stroke-105")])]});
            var Q49;
            Q49=makeQuery(id+"F1.opExtrude","SWEPT_FACE",FACE,{"disambiguationData":[OSD([sQuery(id+"F0.wireOp",EDGE,"E0.sketch_text.stroke-116")])]});
            var Q50;
            Q50=makeQuery(id+"F1.opExtrude","SWEPT_FACE",FACE,{"disambiguationData":[OSD([sQuery(id+"F0.wireOp",EDGE,"E0.sketch_text.stroke-117"),sQuery(id+"F0.wireOp",EDGE,"E0.sketch_text.stroke-118")])]});
            var Q51;
            Q51=makeQuery(id+"F1.opExtrude","SWEPT_FACE",FACE,{"disambiguationData":[OSD([sQuery(id+"F0.wireOp",EDGE,"E0.sketch_text.stroke-110"),sQuery(id+"F0.wireOp",EDGE,"E0.sketch_text.stroke-111")])]});
            var Q52;
            Q52=makeQuery(id+"F1.opExtrude","SWEPT_FACE",FACE,{"disambiguationData":[OSD([sQuery(id+"F0.wireOp",EDGE,"E0.sketch_text.stroke-97")])]});
            var Q53;
            Q53=makeQuery(id+"F1.opExtrude","SWEPT_FACE",FACE,{"disambiguationData":[OSD([sQuery(id+"F0.wireOp",EDGE,"E0.sketch_text.stroke-132")])]});
            var Q54;
            Q54=makeQuery(id+"F1.opExtrude","SWEPT_FACE",FACE,{"disambiguationData":[OSD([sQuery(id+"F0.wireOp",EDGE,"E0.sketch_text.stroke-175")])]});
            var Q55;
            Q55=makeQuery(id+"F1.opExtrude","SWEPT_FACE",FACE,{"disambiguationData":[OSD([sQuery(id+"F0.wireOp",EDGE,"E0.sketch_text.stroke-158")])]});
            var Q56;
            Q56=makeQuery(id+"F1.opExtrude","SWEPT_FACE",FACE,{"disambiguationData":[OSD([sQuery(id+"F0.wireOp",EDGE,"E0.sketch_text.stroke-167"),sQuery(id+"F0.wireOp",EDGE,"E0.sketch_text.stroke-168")])]});
            var Q57;
            Q57=makeQuery(id+"F1.opExtrude","SWEPT_FACE",FACE,{"disambiguationData":[OSD([sQuery(id+"F0.wireOp",EDGE,"E0.sketch_text.stroke-162")])]});
            var Q58;
            Q58=makeQuery(id+"F1.opExtrude","SWEPT_FACE",FACE,{"disambiguationData":[OSD([sQuery(id+"F0.wireOp",EDGE,"E0.sketch_text.stroke-164")])]});
            var Q59;
            Q59=makeQuery(id+"F1.opExtrude","SWEPT_FACE",FACE,{"disambiguationData":[OSD([sQuery(id+"F0.wireOp",EDGE,"E0.sketch_text.stroke-125")])]});
            var Q60;
            Q60=makeQuery(id+"F1.opExtrude","SWEPT_FACE",FACE,{"disambiguationData":[OSD([sQuery(id+"F0.wireOp",EDGE,"E0.sketch_text.stroke-127")])]});
            var Q61;
            Q61=makeQuery(id+"F1.opExtrude","SWEPT_FACE",FACE,{"disambiguationData":[OSD([sQuery(id+"F0.wireOp",EDGE,"E0.sketch_text.stroke-129")])]});
            var Q62;
            Q62=makeQuery(id+"F1.opExtrude","SWEPT_FACE",FACE,{"disambiguationData":[OSD([sQuery(id+"F0.wireOp",EDGE,"E0.sketch_text.stroke-166")])]});
            var Q63;
            Q63=makeQuery(id+"F1.opExtrude","SWEPT_FACE",FACE,{"disambiguationData":[OSD([sQuery(id+"F0.wireOp",EDGE,"E0.sketch_text.stroke-178")])]});
            var Q64;
            Q64=makeQuery(id+"F1.opExtrude","SWEPT_FACE",FACE,{"disambiguationData":[OSD([sQuery(id+"F0.wireOp",EDGE,"E0.sketch_text.stroke-192")])]});
            var Q65;
            Q65=makeQuery(id+"F1.opExtrude","SWEPT_FACE",FACE,{"disambiguationData":[OSD([sQuery(id+"F0.wireOp",EDGE,"E0.sketch_text.stroke-183")])]});
            var Q66;
            Q66=makeQuery(id+"F1.opExtrude","SWEPT_FACE",FACE,{"disambiguationData":[OSD([sQuery(id+"F0.wireOp",EDGE,"E0.sketch_text.stroke-191")])]});
            var Q67;
            Q67=makeQuery(id+"F1.opExtrude","SWEPT_FACE",FACE,{"disambiguationData":[OSD([sQuery(id+"F0.wireOp",EDGE,"E0.sketch_text.stroke-189")])]});
            var Q68;
            Q68=makeQuery(id+"F1.opExtrude","SWEPT_FACE",FACE,{"disambiguationData":[OSD([sQuery(id+"F0.wireOp",EDGE,"E0.sketch_text.stroke-181")])]});
            var Q69;
            Q69=makeQuery(id+"F1.opExtrude","SWEPT_FACE",FACE,{"disambiguationData":[OSD([sQuery(id+"F0.wireOp",EDGE,"E0.sketch_text.stroke-179")])]});
            var Q70;
            Q70=makeQuery(id+"F4.opFillet","BLEND_EDGE",EDGE,{"blendedFrom":[makeQuery(id+"F3.opExtrude","CAP_EDGE",EDGE,{"disambiguationData":[OSD([sQuery(id+"F2.wireOp",EDGE,"E1.top")])],"isStart":true}),makeQuery(id+"F3.opExtrude","CAP_EDGE",EDGE,{"disambiguationData":[OSD([sQuery(id+"F2.wireOp",EDGE,"E1.right")])],"isStart":true})],"blendedInto":[]});
            var Q71;
            Q71=makeQuery(id+"F4.opFillet","BLEND_EDGE",EDGE,{"blendedFrom":[makeQuery(id+"F3.opExtrude","CAP_EDGE",EDGE,{"disambiguationData":[OSD([sQuery(id+"F2.wireOp",EDGE,"E1.bottom")])],"isStart":true}),makeQuery(id+"F3.opExtrude","CAP_EDGE",EDGE,{"disambiguationData":[OSD([sQuery(id+"F2.wireOp",EDGE,"E1.right")])],"isStart":true})],"blendedInto":[]});
            var Q72;
            Q72=makeQuery(id+"F4.opFillet","BLEND_EDGE",EDGE,{"blendedFrom":[makeQuery(id+"F3.opExtrude","CAP_EDGE",EDGE,{"disambiguationData":[OSD([sQuery(id+"F2.wireOp",EDGE,"E1.bottom")])],"isStart":true}),makeQuery(id+"F3.opExtrude","CAP_EDGE",EDGE,{"disambiguationData":[OSD([sQuery(id+"F2.wireOp",EDGE,"E1.left")])],"isStart":true})],"blendedInto":[]});
            var Q73;
            Q73=makeQuery(id+"F4.opFillet","BLEND_EDGE",EDGE,{"blendedFrom":[makeQuery(id+"F3.opExtrude","CAP_EDGE",EDGE,{"disambiguationData":[OSD([sQuery(id+"F2.wireOp",EDGE,"E1.top")])],"isStart":true}),makeQuery(id+"F3.opExtrude","CAP_EDGE",EDGE,{"disambiguationData":[OSD([sQuery(id+"F2.wireOp",EDGE,"E1.left")])],"isStart":true})],"blendedInto":[]});
            fillet(context, id + "F5", {"entities" : qUnion([Q0, Q1, Q2, Q3, Q4, Q5, Q6, Q7, Q8, Q9, Q10, Q11, Q12, Q13, Q14, Q15, Q16, Q17, Q18, Q19, Q20, Q21, Q22, Q23, Q24, Q25, Q26, Q27, Q28, Q29, Q30, Q31, Q32, Q33, Q34, Q35, Q36, Q37, Q38, Q39, Q40, Q41, Q42, Q43, Q44, Q45, Q46, Q47, Q48, Q49, Q50, Q51, Q52, Q53, Q54, Q55, Q56, Q57, Q58, Q59, Q60, Q61, Q62, Q63, Q64, Q65, Q66, Q67, Q68, Q69, Q70, Q71, Q72, Q73]), "radius" : 1 * mm, "tangentPropagation" : true, "allowEdgeOverflow" : false});
        }
    });
